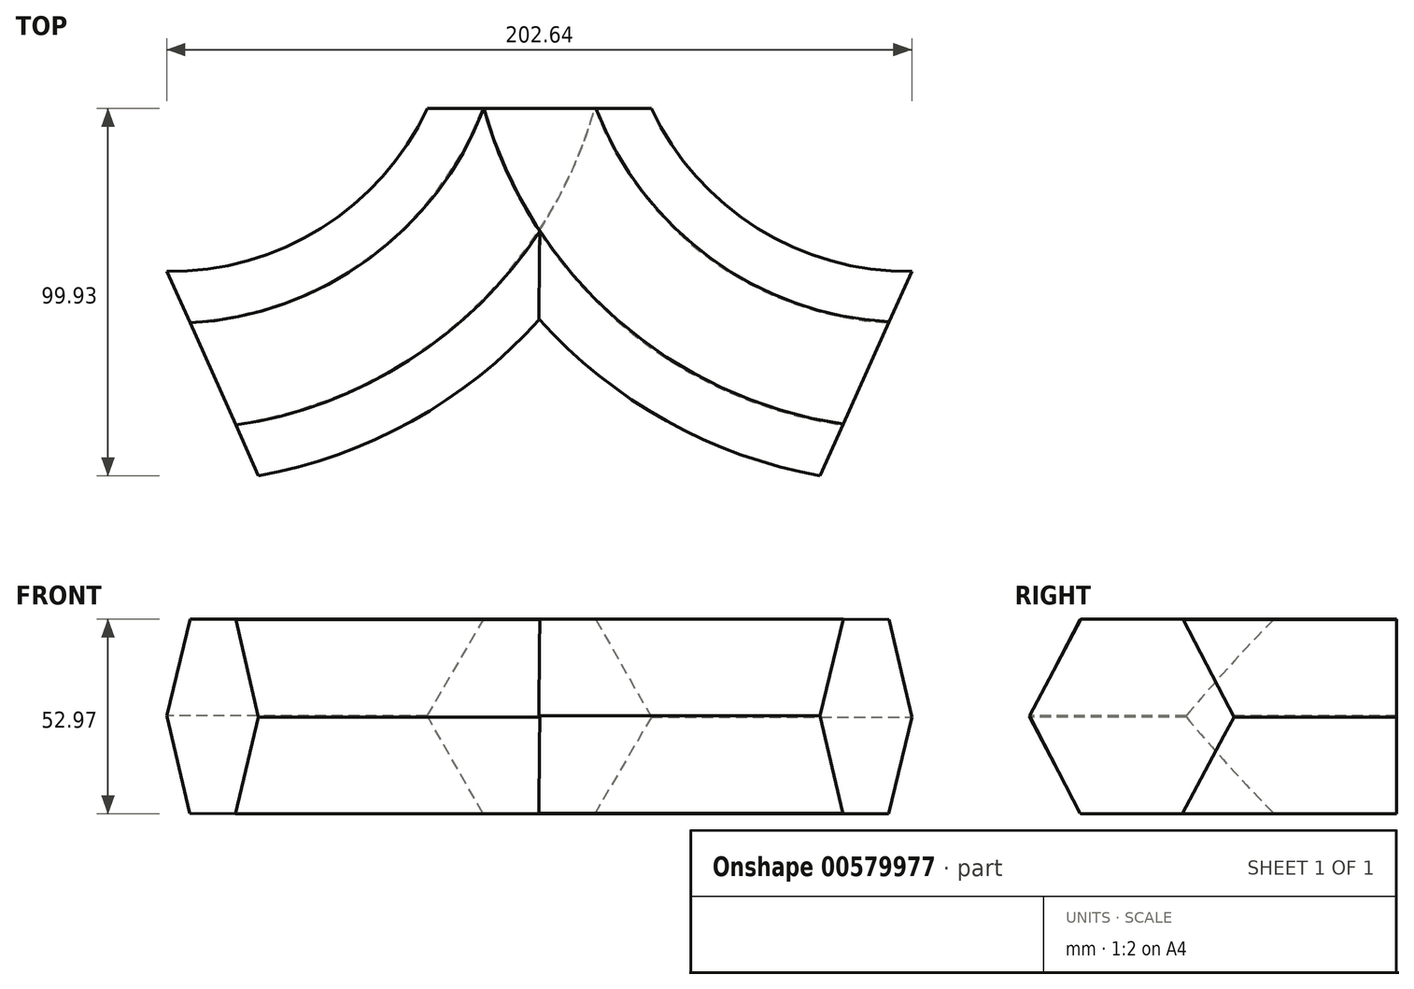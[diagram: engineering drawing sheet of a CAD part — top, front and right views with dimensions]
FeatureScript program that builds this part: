
annotation { "Feature Type Name" : "Feature", "Feature Type Description" : "" }
export const myFeature = defineFeature(function(context is Context, id is Id, definition is map)
    precondition{}
    {
        {
            var Q0;
            Q0=qCreatedBy(makeId("Front.planeOp"),FACE);
            var sketch = newSketch(context, id + "F0", { "sketchPlane" : qUnion([Q0])});
            skCircle(sketch, "E0.cCircle", {"center": v(0, 26.89) * mm, "radius": 26.4 * mm, "construction": true});
            skLineSegment(sketch, "E0.0", {"start": v(-15.4, 0.58) * mm, "end": v(-30.48, 27.07) * mm});
            skLineSegment(sketch, "E0.1", {"start": v(-30.48, 27.07) * mm, "end": v(-15.08, 53.37) * mm});
            skLineSegment(sketch, "E0.2", {"start": v(-15.08, 53.37) * mm, "end": v(15.4, 53.2) * mm});
            skLineSegment(sketch, "E0.3", {"start": v(15.4, 53.2) * mm, "end": v(30.48, 26.7) * mm});
            skLineSegment(sketch, "E0.4", {"start": v(30.48, 26.7) * mm, "end": v(15.08, 0.4) * mm});
            skLineSegment(sketch, "E0.5", {"start": v(15.08, 0.4) * mm, "end": v(-15.4, 0.58) * mm});
            skPoint(sketch, "E0.0.midPoint", {"position": v(-22.94, 13.82) * mm});
            skSolve(sketch);
        }
        {
            var Q0;
            Q0=qCreatedBy(makeId("Top.planeOp"),FACE);
            var sketch = newSketch(context, id + "F1", { "sketchPlane" : qUnion([Q0])});
            skArc(sketch, "E1", {"start": v(-88.86, -72.11) * mm, "mid": v(-33.77, -49.2) * mm, "end": v(0, 0) * mm});
            skArc(sketch, "E2.MirrorCS", {"start": v(88.86, -72.11) * mm, "mid": v(33.77, -49.2) * mm, "end": v(0, 0) * mm});
            skSolve(sketch);
        }
        {
            var Q0;
            Q0=makeQuery(id+"F0.imprint","IMPRINT",FACE,{"disambiguationData":[TD([[makeQuery(id+"F0.imprint","IMPRINT",EDGE,{"derivedFrom":sQuery(id+"F0.wireOp",EDGE,"E0.0")}),-1.0]])]});
            var Q1;
            Q1=sQuery(id+"F1.wireOp",EDGE,"E1");
            sweep(context, id + "F2", {"profiles" : qUnion([Q0]), "path" : qUnion([Q1])});
        }
        {
            var Q0;
            Q0=makeQuery(id+"F0.imprint","IMPRINT",FACE,{"disambiguationData":[TD([[makeQuery(id+"F0.imprint","IMPRINT",EDGE,{"derivedFrom":sQuery(id+"F0.wireOp",EDGE,"E0.0")}),-1.0]])]});
            var Q1;
            Q1=sQuery(id+"F1.wireOp",EDGE,"E2.MirrorCS");
            sweep(context, id + "F3", {"operationType" : NewBodyOperationType.ADD, "profiles" : qUnion([Q0]), "path" : qUnion([Q1])});
        }
    });
